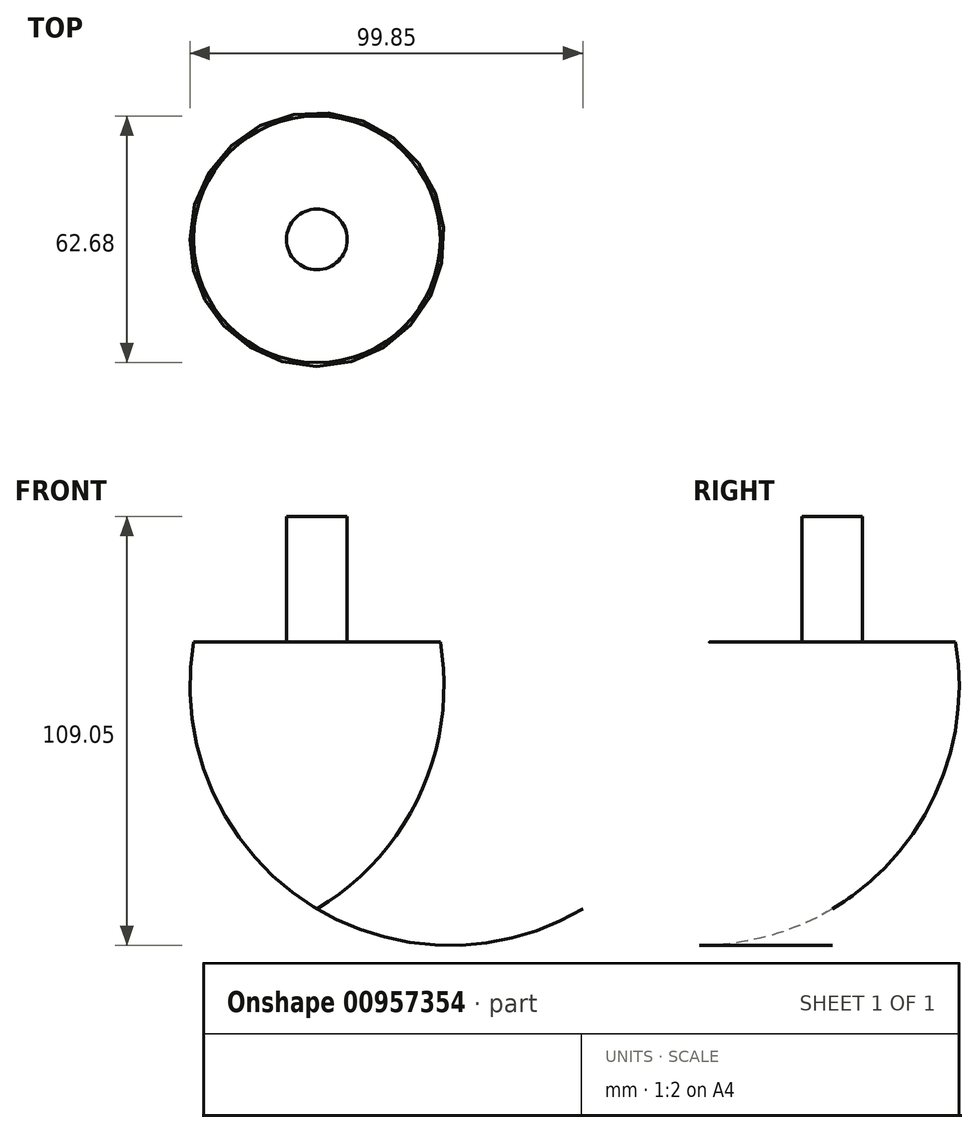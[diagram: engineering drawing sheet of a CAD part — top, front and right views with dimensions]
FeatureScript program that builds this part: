
annotation { "Feature Type Name" : "Feature", "Feature Type Description" : "" }
export const myFeature = defineFeature(function(context is Context, id is Id, definition is map)
    precondition{}
    {
        {
            var Q0;
            Q0=qCreatedBy(makeId("Front.planeOp"),FACE);
            var sketch = newSketch(context, id + "F0", { "sketchPlane" : qUnion([Q0])});
            skLineSegment(sketch, "E0", {"start": v(0, 48.49) * mm, "end": v(7.7, 48.49) * mm});
            skLineSegment(sketch, "E1", {"start": v(7.7, 48.49) * mm, "end": v(7.7, 16.53) * mm});
            skLineSegment(sketch, "E2", {"start": v(7.7, 16.53) * mm, "end": v(31.34, 16.53) * mm});
            skArc(sketch, "E3", {"start": v(0, -51.27) * mm, "mid": v(26.17, -22.22) * mm, "end": v(31.34, 16.53) * mm});
            skLineSegment(sketch, "E4", {"start": v(0, 48.49) * mm, "end": v(0, -51.27) * mm});
            skLineSegment(sketch, "E5", {"start": v(7.7, 16.53) * mm, "end": v(17.69, 29.41) * mm});
            skLineSegment(sketch, "E6", {"start": v(17.69, 29.41) * mm, "end": v(7.7, 14.74) * mm});
            skLineSegment(sketch, "E7", {"start": v(17.69, 29.41) * mm, "end": v(17.69, 16.53) * mm});
            skSolve(sketch);
        }
        {
            var Q0;
            Q0=makeQuery(id+"F0.imprint","IMPRINT",FACE,{"disambiguationData":[TD([[makeQuery(id+"F0.imprint","IMPRINT",EDGE,{"derivedFrom":sQuery(id+"F0.wireOp",EDGE,"E0")}),-1.0]])]});
            var Q1;
            Q1=sQuery(id+"F0.wireOp",EDGE,"E4");
            revolve(context, id + "F1", {"surfaceOperationType" : NewSurfaceOperationType.NEW, "entities" : qUnion([Q0]), "axis" : qUnion([Q1]), "revolveType" : RevolveType.FULL});
        }
    });
